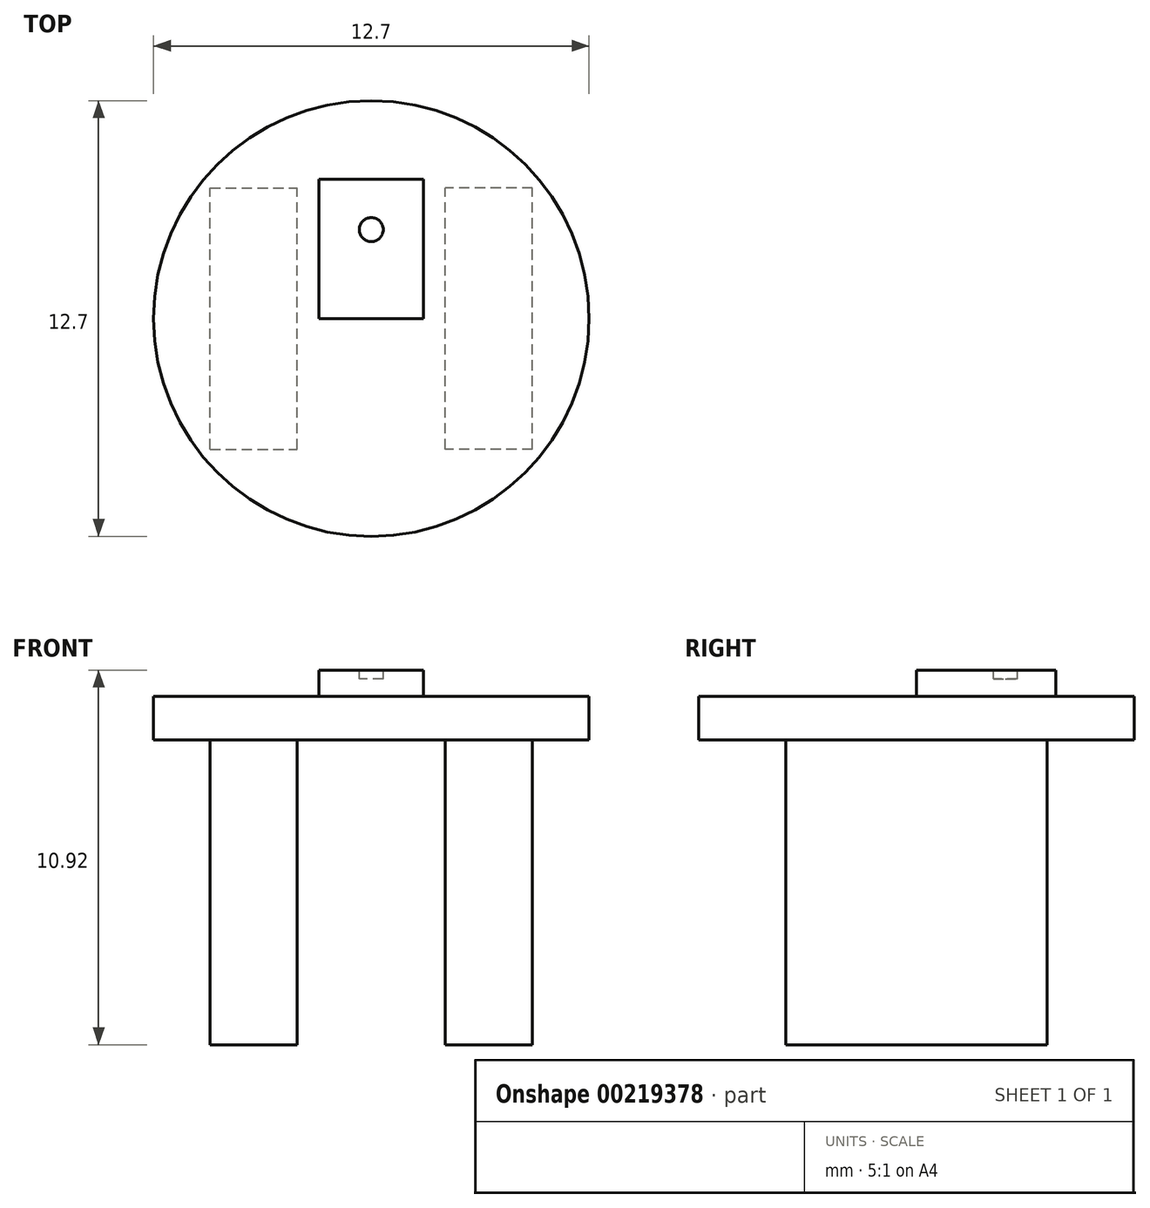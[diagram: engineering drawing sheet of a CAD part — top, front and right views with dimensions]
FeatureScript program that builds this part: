
annotation { "Feature Type Name" : "Feature", "Feature Type Description" : "" }
export const myFeature = defineFeature(function(context is Context, id is Id, definition is map)
    precondition{}
    {
        {
            var Q0;
            Q0=qCreatedBy(makeId("Top.planeOp"),FACE);
            var sketch = newSketch(context, id + "F0", { "sketchPlane" : qUnion([Q0])});
            skCircle(sketch, "E0", {"center": v(0, 0) * mm, "radius": 6.35 * mm});
            skSolve(sketch);
        }
        {
            var Q0;
            Q0 = qSketchRegion(id + "F0", true);
            extrude(context, id + "F1", {"entities" : qUnion([Q0]), "depth" : 1.27 * mm});
        }
        {
            var Q0;
            Q0=makeQuery(id+"F1.opExtrude","CAP_FACE",FACE,{"disambiguationData":[OSD([sQuery(id+"F0.wireOp",EDGE,"E0")])],"isStart":false});
            var sketch = newSketch(context, id + "F2", { "sketchPlane" : qUnion([Q0])});
            skLineSegment(sketch, "E1.bottom", {"start": v(-1.52, 0) * mm, "end": v(1.52, 0) * mm});
            skLineSegment(sketch, "E1.top", {"start": v(-1.52, 4.06) * mm, "end": v(1.52, 4.06) * mm});
            skLineSegment(sketch, "E1.left", {"start": v(-1.52, 0) * mm, "end": v(-1.52, 4.06) * mm});
            skLineSegment(sketch, "E1.right", {"start": v(1.52, 0) * mm, "end": v(1.52, 4.06) * mm});
            skSolve(sketch);
        }
        {
            var Q0;
            Q0 = qSketchRegion(id + "F2", true);
            extrude(context, id + "F3", {"entities" : qUnion([Q0]), "operationType" : NewBodyOperationType.ADD, "depth" : 0.76 * mm});
        }
        {
            var Q0;
            Q0=makeQuery(id+"F3.opExtrude","CAP_FACE",FACE,{"disambiguationData":[OSD([sQuery(id+"F2.wireOp",EDGE,"E1.bottom"),sQuery(id+"F2.wireOp",EDGE,"E1.top"),sQuery(id+"F2.wireOp",EDGE,"E1.left"),sQuery(id+"F2.wireOp",EDGE,"E1.right")])],"isStart":false});
            var sketch = newSketch(context, id + "F4", { "sketchPlane" : qUnion([Q0])});
            skCircle(sketch, "E2", {"center": v(0, 2.6) * mm, "radius": 0.35 * mm});
            skSolve(sketch);
        }
        {
            var Q0;
            Q0 = qSketchRegion(id + "F4", true);
            extrude(context, id + "F5", {"entities" : qUnion([Q0]), "operationType" : NewBodyOperationType.REMOVE, "oppositeDirection" : true, "depth" : 0.25 * mm});
        }
        {
            var Q0;
            Q0=makeQuery(id+"F1.opExtrude","CAP_FACE",FACE,{"disambiguationData":[OSD([sQuery(id+"F0.wireOp",EDGE,"E0")])],"isStart":true});
            var sketch = newSketch(context, id + "F6", { "sketchPlane" : qUnion([Q0])});
            skLineSegment(sketch, "E3.bottom", {"start": v(-4.7, 3.81) * mm, "end": v(-2.16, 3.81) * mm});
            skLineSegment(sketch, "E3.top", {"start": v(-4.7, -3.81) * mm, "end": v(-2.16, -3.8) * mm});
            skLineSegment(sketch, "E3.left", {"start": v(-4.7, 3.81) * mm, "end": v(-4.7, -3.81) * mm});
            skLineSegment(sketch, "E3.right", {"start": v(-2.16, 3.81) * mm, "end": v(-2.16, -3.8) * mm});
            skSolve(sketch);
        }
        {
            var Q0;
            Q0 = qSketchRegion(id + "F6", true);
            extrude(context, id + "F7", {"entities" : qUnion([Q0]), "operationType" : NewBodyOperationType.ADD, "depth" : 8.9 * mm});
        }
        {
            var Q0;
            Q0=makeQuery(id+"F1.opExtrude","SWEPT_BODY",BODY,{"disambiguationData":[OSD([sQuery(id+"F0.wireOp",EDGE,"E0")])]});
            var Q1;
            Q1=qCreatedBy(makeId("Right.planeOp"),FACE);
            mirror(context, id + "F8", {"operationType" : NewBodyOperationType.ADD, "entities" : qUnion([Q0]), "mirrorPlane" : qUnion([Q1])});
        }
    });
